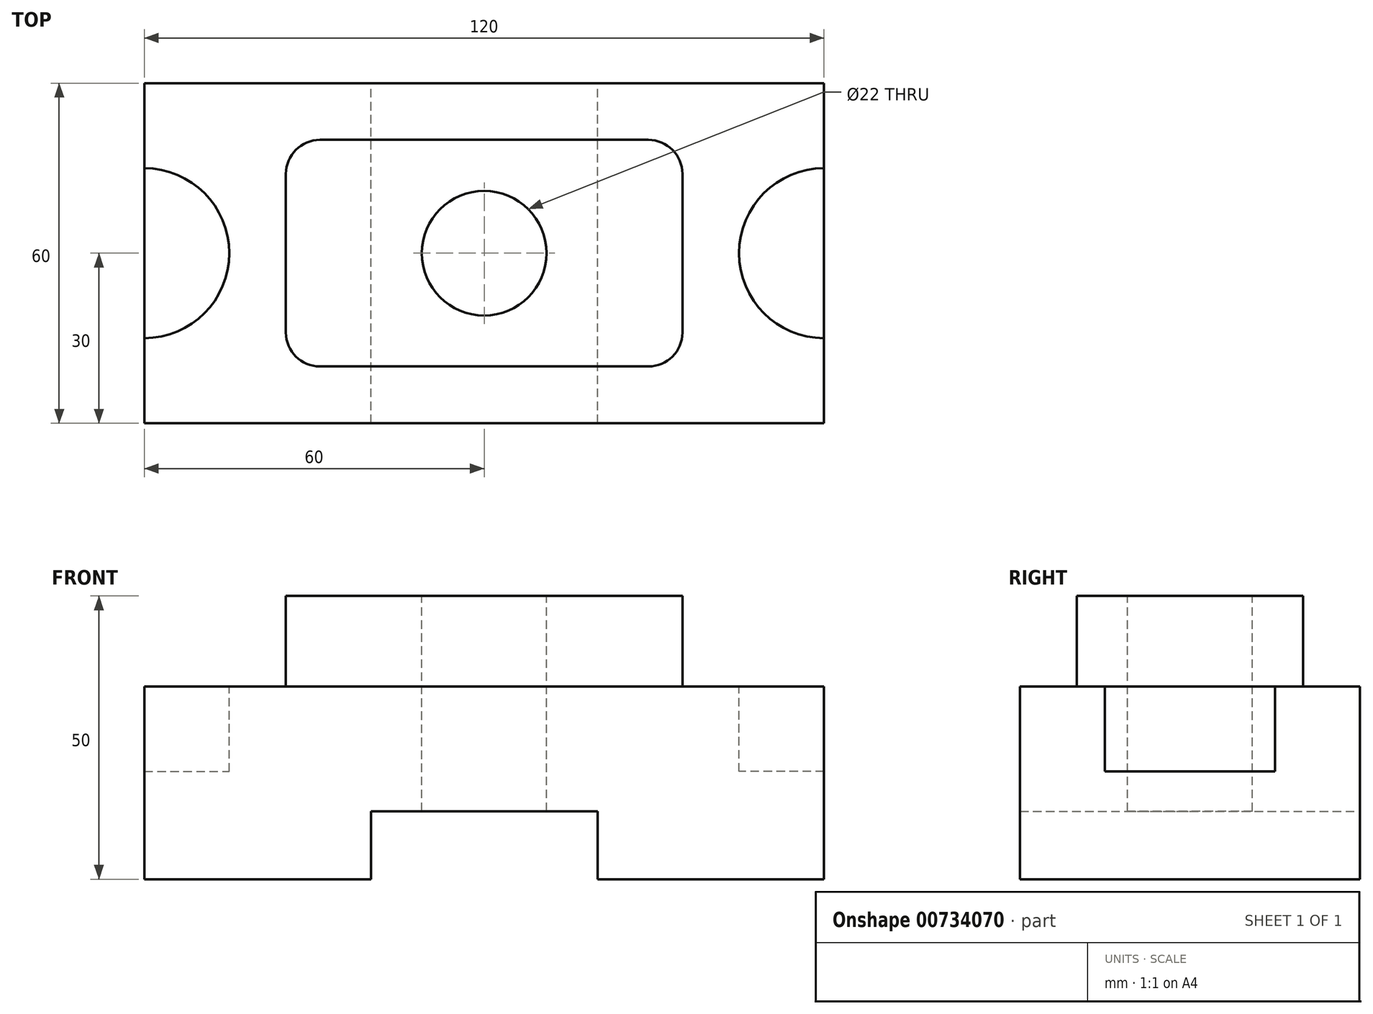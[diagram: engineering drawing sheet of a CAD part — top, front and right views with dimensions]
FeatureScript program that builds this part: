
annotation { "Feature Type Name" : "Feature", "Feature Type Description" : "" }
export const myFeature = defineFeature(function(context is Context, id is Id, definition is map)
    precondition{}
    {
        {
            var Q0;
            Q0=qCreatedBy(makeId("Top.planeOp"),FACE);
            var sketch = newSketch(context, id + "F0", { "sketchPlane" : qUnion([Q0])});
            skLineSegment(sketch, "E0.bottom", {"start": v(-60, -30) * mm, "end": v(60, -30) * mm});
            skLineSegment(sketch, "E0.top", {"start": v(-60, 30) * mm, "end": v(60, 30) * mm});
            skLineSegment(sketch, "E0.left", {"start": v(-60, -30) * mm, "end": v(-60, 30) * mm});
            skLineSegment(sketch, "E0.right", {"start": v(60, -30) * mm, "end": v(60, 30) * mm});
            skPoint(sketch, "E0.middle", {"position": v(0, 0) * mm});
            skSolve(sketch);
        }
        {
            var Q0;
            Q0=makeQuery(id+"F0.imprint","IMPRINT",FACE,{"disambiguationData":[TD([[makeQuery(id+"F0.imprint","IMPRINT",EDGE,{"derivedFrom":sQuery(id+"F0.wireOp",EDGE,"E0.bottom")}),1.0]])]});
            extrude(context, id + "F1", {"entities" : qUnion([Q0]), "depth" : 34 * mm, "offsetDistance" : 25 * mm});
        }
        {
            var Q0;
            Q0=makeQuery(id+"F1.opExtrude","CAP_FACE",FACE,{"disambiguationData":[OSD([sQuery(id+"F0.wireOp",EDGE,"E0.bottom"),sQuery(id+"F0.wireOp",EDGE,"E0.top"),sQuery(id+"F0.wireOp",EDGE,"E0.left"),sQuery(id+"F0.wireOp",EDGE,"E0.right")])],"isStart":false});
            var sketch = newSketch(context, id + "F2", { "sketchPlane" : qUnion([Q0])});
            skCircle(sketch, "E1", {"center": v(-60, 0) * mm, "radius": 15 * mm});
            skCircle(sketch, "E2", {"center": v(60, 0) * mm, "radius": 15 * mm});
            skSolve(sketch);
        }
        {
            var Q0;
            Q0 = qSketchRegion(id + "F2", true);
            extrude(context, id + "F3", {"entities" : qUnion([Q0]), "operationType" : NewBodyOperationType.REMOVE, "oppositeDirection" : true, "depth" : 15 * mm, "offsetDistance" : 25 * mm});
        }
        {
            var Q0;
            Q0=makeQuery(id+"F1.opExtrude","CAP_FACE",FACE,{"disambiguationData":[OSD([sQuery(id+"F0.wireOp",EDGE,"E0.bottom"),sQuery(id+"F0.wireOp",EDGE,"E0.top"),sQuery(id+"F0.wireOp",EDGE,"E0.left"),sQuery(id+"F0.wireOp",EDGE,"E0.right")])],"isStart":false});
            var sketch = newSketch(context, id + "F4", { "sketchPlane" : qUnion([Q0])});
            skLineSegment(sketch, "E3", {"start": v(-60, -30) * mm, "end": v(-35, -30) * mm});
            skLineSegment(sketch, "E4", {"start": v(-29, -20) * mm, "end": v(29, -20) * mm});
            skLineSegment(sketch, "E5", {"start": v(35, -14) * mm, "end": v(35, 14) * mm});
            skLineSegment(sketch, "E6", {"start": v(29, 20) * mm, "end": v(-29, 20) * mm});
            skLineSegment(sketch, "E7", {"start": v(-35, 14) * mm, "end": v(-35, -14) * mm});
            skPoint(sketch, "E8.visualSharp", {"position": v(-35, 20) * mm});
            skArc(sketch, "E8.filletArc", {"start": v(-29, 20) * mm, "mid": v(-33.24, 18.24) * mm, "end": v(-35, 14) * mm});
            skPoint(sketch, "E9.visualSharp", {"position": v(35, 20) * mm});
            skArc(sketch, "E9.filletArc", {"start": v(35, 14) * mm, "mid": v(33.24, 18.24) * mm, "end": v(29, 20) * mm});
            skPoint(sketch, "E10.visualSharp", {"position": v(35, -20) * mm});
            skArc(sketch, "E10.filletArc", {"start": v(29, -20) * mm, "mid": v(33.24, -18.24) * mm, "end": v(35, -14) * mm});
            skPoint(sketch, "E11.visualSharp", {"position": v(-35, -20) * mm});
            skArc(sketch, "E11.filletArc", {"start": v(-35, -14) * mm, "mid": v(-33.24, -18.24) * mm, "end": v(-29, -20) * mm});
            skSolve(sketch);
        }
        {
            var Q0;
            Q0=makeQuery(id+"F4.imprint","IMPRINT",FACE,{"disambiguationData":[TD([[makeQuery(id+"F4.imprint","IMPRINT",EDGE,{"derivedFrom":sQuery(id+"F4.wireOp",EDGE,"E4")}),1.0]])]});
            extrude(context, id + "F5", {"entities" : qUnion([Q0]), "operationType" : NewBodyOperationType.ADD, "depth" : 16 * mm, "offsetDistance" : 25 * mm});
        }
        {
            var Q0;
            Q0=makeQuery(id+"F5.opExtrude","CAP_FACE",FACE,{"disambiguationData":[OSD([sQuery(id+"F4.wireOp",EDGE,"E4"),sQuery(id+"F4.wireOp",EDGE,"E5"),sQuery(id+"F4.wireOp",EDGE,"E6"),sQuery(id+"F4.wireOp",EDGE,"E7"),sQuery(id+"F4.wireOp",EDGE,"E8.filletArc"),sQuery(id+"F4.wireOp",EDGE,"E9.filletArc"),sQuery(id+"F4.wireOp",EDGE,"E10.filletArc"),sQuery(id+"F4.wireOp",EDGE,"E11.filletArc")])],"isStart":false});
            var sketch = newSketch(context, id + "F6", { "sketchPlane" : qUnion([Q0])});
            skCircle(sketch, "E12", {"center": v(0, 0) * mm, "radius": 11 * mm});
            skSolve(sketch);
        }
        {
            var Q0;
            Q0 = qSketchRegion(id + "F6", true);
            extrude(context, id + "F7", {"entities" : qUnion([Q0]), "operationType" : NewBodyOperationType.REMOVE, "oppositeDirection" : true, "depth" : 38 * mm, "offsetDistance" : 25 * mm});
        }
        {
            var Q0;
            Q0=makeQuery(id+"F1.opExtrude","SWEPT_FACE",FACE,{"disambiguationData":[OSD([sQuery(id+"F0.wireOp",EDGE,"E0.top")])]});
            var sketch = newSketch(context, id + "F8", { "sketchPlane" : qUnion([Q0])});
            skLineSegment(sketch, "E13", {"start": v(-60, 0) * mm, "end": v(-20, 0) * mm});
            skLineSegment(sketch, "E14", {"start": v(-20, 0) * mm, "end": v(-20, 12) * mm});
            skLineSegment(sketch, "E15", {"start": v(-20, 12) * mm, "end": v(20, 12) * mm});
            skLineSegment(sketch, "E16", {"start": v(20, 12) * mm, "end": v(20, 0) * mm});
            skLineSegment(sketch, "E17", {"start": v(20, 0) * mm, "end": v(-20, 0) * mm});
            skSolve(sketch);
        }
        {
            var Q0;
            Q0 = qSketchRegion(id + "F8", true);
            extrude(context, id + "F9", {"entities" : qUnion([Q0]), "operationType" : NewBodyOperationType.REMOVE, "oppositeDirection" : true, "depth" : 60 * mm, "offsetDistance" : 25 * mm});
        }
    });
